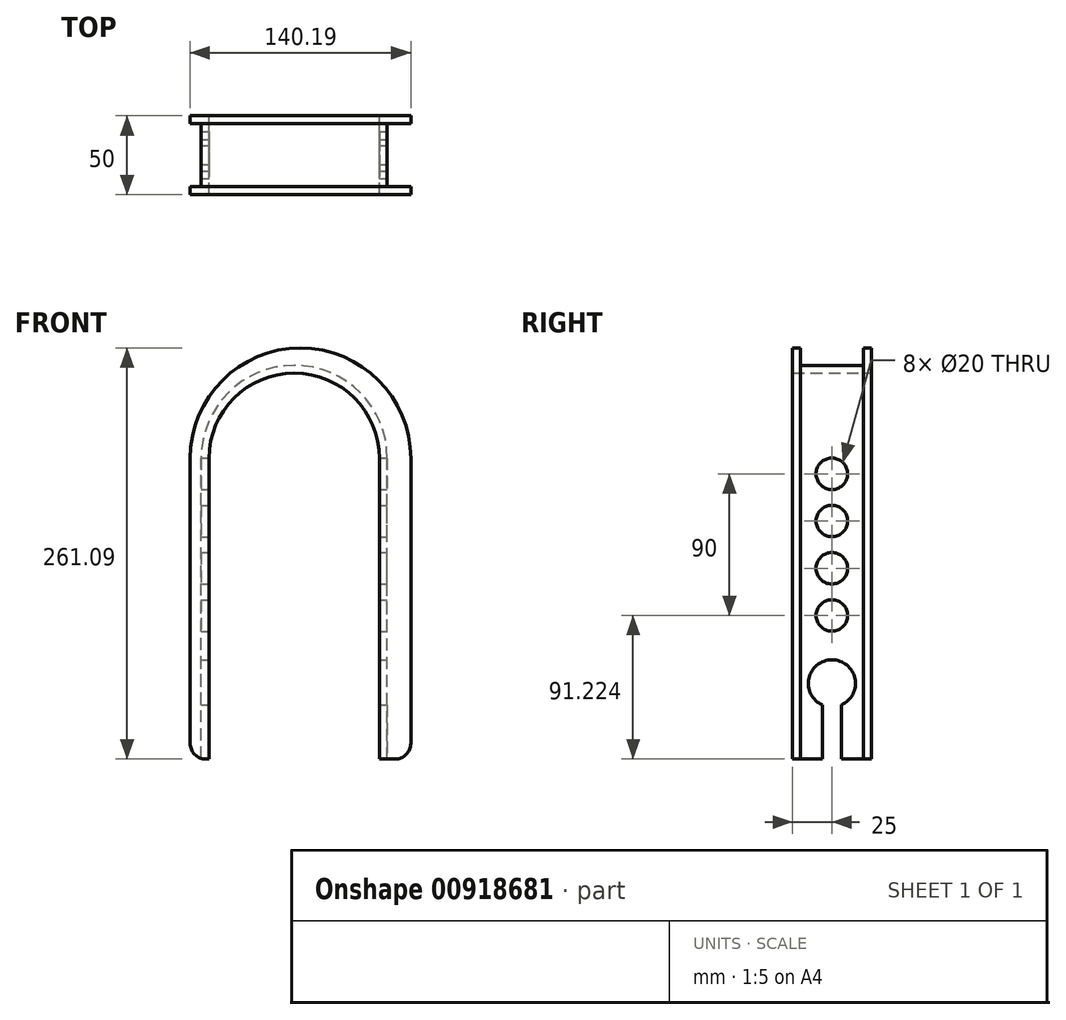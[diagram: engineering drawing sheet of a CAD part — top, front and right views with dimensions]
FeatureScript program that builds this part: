
annotation { "Feature Type Name" : "Feature", "Feature Type Description" : "" }
export const myFeature = defineFeature(function(context is Context, id is Id, definition is map)
    precondition{}
    {
        {
            var Q0;
            Q0=qCreatedBy(makeId("Front.planeOp"),FACE);
            var sketch = newSketch(context, id + "F0", { "sketchPlane" : qUnion([Q0])});
            skLineSegment(sketch, "E0", {"start": v(-68.1, -115.24) * mm, "end": v(-68.1, 65.76) * mm});
            skLineSegment(sketch, "E1", {"start": v(-56.1, -125.24) * mm, "end": v(-56.1, 65.76) * mm});
            skLineSegment(sketch, "E2", {"start": v(52.08, -125.24) * mm, "end": v(52.08, 65.76) * mm});
            skLineSegment(sketch, "E3", {"start": v(72.08, -115.24) * mm, "end": v(72.08, 65.76) * mm});
            skArc(sketch, "E4", {"start": v(52.08, 65.76) * mm, "mid": v(-2.01, 119.85) * mm, "end": v(-56.1, 65.76) * mm});
            skArc(sketch, "E5", {"start": v(72.08, 65.76) * mm, "mid": v(1.99, 135.85) * mm, "end": v(-68.1, 65.76) * mm});
            skLineSegment(sketch, "E6", {"start": v(-58.1, -125.24) * mm, "end": v(-56.1, -125.24) * mm});
            skLineSegment(sketch, "E7", {"start": v(52.08, -125.24) * mm, "end": v(62.08, -125.24) * mm});
            skPoint(sketch, "E8.visualSharp", {"position": v(-68.1, -125.24) * mm});
            skArc(sketch, "E8.filletArc", {"start": v(-68.1, -115.24) * mm, "mid": v(-65.18, -122.31) * mm, "end": v(-58.1, -125.24) * mm});
            skPoint(sketch, "E9.visualSharp", {"position": v(72.08, -125.24) * mm});
            skArc(sketch, "E9.filletArc", {"start": v(62.08, -125.24) * mm, "mid": v(69.15, -122.31) * mm, "end": v(72.08, -115.24) * mm});
            skLineSegment(sketch, "E10", {"start": v(-68.1, 65.76) * mm, "end": v(75.19, 65.76) * mm, "construction": true});
            skLineSegment(sketch, "E11", {"start": v(75.19, 65.76) * mm, "end": v(-68.1, 65.76) * mm, "construction": true});
            skLineSegment(sketch, "E12", {"start": v(-95.5, -125.24) * mm, "end": v(86.96, -125.24) * mm, "construction": true});
            skSolve(sketch);
        }
        {
            var Q0;
            Q0 = qSketchRegion(id + "F0", true);
            extrude(context, id + "F1", {"entities" : qUnion([Q0]), "depth" : 50 * mm, "offsetDistance" : 25 * mm});
        }
        {
            var Q0;
            Q0=makeQuery(id+"F1.opExtrude","SWEPT_FACE",FACE,{"disambiguationData":[OSD([sQuery(id+"F0.wireOp",EDGE,"E0")])]});
            var Q1;
            Q1=makeQuery(id+"F1.opExtrude","SWEPT_FACE",FACE,{"disambiguationData":[OSD([sQuery(id+"F0.wireOp",EDGE,"E5")])]});
            var Q2;
            Q2=makeQuery(id+"F1.opExtrude","SWEPT_FACE",FACE,{"disambiguationData":[OSD([sQuery(id+"F0.wireOp",EDGE,"E3")])]});
            shell(context, id + "F2", {"entities" : qUnion([Q0, Q1, Q2]), "thickness" : 5 * mm});
        }
        {
            var Q0;
            Q0=makeQuery(id+"F2.opShell","OFFSET_FACE",FACE,{"disambiguationData":[OSD([sQuery(id+"F0.wireOp",EDGE,"E2")])]});
            var sketch = newSketch(context, id + "F3", { "sketchPlane" : qUnion([Q0])});
            skPoint(sketch, "E13.centerSnap0", {"position": v(-25, -120.24) * mm});
            skLineSegment(sketch, "E14", {"start": v(9.24, -77.17) * mm, "end": v(-58.42, -77.17) * mm, "construction": true});
            skPoint(sketch, "E13.center.orphan", {"position": v(-25, -77.17) * mm});
            skArc(sketch, "E15", {"start": v(-19, -90.92) * mm, "mid": v(-25, -62.17) * mm, "end": v(-31, -90.92) * mm});
            skLineSegment(sketch, "E16", {"start": v(-31, -90.92) * mm, "end": v(-31, -125.83) * mm});
            skLineSegment(sketch, "E17", {"start": v(-19, -90.92) * mm, "end": v(-19, -125.83) * mm});
            skSolve(sketch);
        }
        {
            var Q0;
            Q0=makeQuery(id+"Fxhhjyly7ikEwcR_1.boolean.opBoolean","MERGE",FACE,{"derivedFrom":[makeQuery(id+"F2.opShell","OFFSET_FACE",FACE,{"disambiguationData":[OSD([sQuery(id+"F0.wireOp",EDGE,"E2")])]})],"fromTools":[makeQuery(id+"Fxhhjyly7ikEwcR_1.opExtrude","CAP_FACE",FACE,{"disambiguationData":[OSD([sQuery(id+"F0.wireOp",EDGE,"E3"),sQuery(id+"F0.wireOp",EDGE,"E7"),sQuery(id+"FfAtlhIJGWQoZcc_1.wireOp",EDGE,"lfH36EOl-3g7w-Wpb9-1w7m-nU63kjSk3KXv"),sQuery(id+"FfAtlhIJGWQoZcc_1.wireOp",EDGE,"4ROan0Rv-7vJr-hjll-RH8p-9FkXIwtYWzqe")])],"isStart":false})]});
            var sketch = newSketch(context, id + "F4", { "sketchPlane" : qUnion([Q0])});
            skCircle(sketch, "E18", {"center": v(-25, 55.98) * mm, "radius": 10 * mm});
            skPoint(sketch, "E18.centerSnap0", {"position": v(-25, 65.76) * mm});
            skCircle(sketch, "E19", {"center": v(-25, 25.98) * mm, "radius": 10 * mm});
            skCircle(sketch, "E20", {"center": v(-25, -4.02) * mm, "radius": 10 * mm});
            skCircle(sketch, "E21", {"center": v(-25, -34.02) * mm, "radius": 10 * mm});
            skSolve(sketch);
        }
        {
            var Q0;
            Q0 = qSketchRegion(id + "F4", true);
            extrude(context, id + "F5", {"entities" : qUnion([Q0]), "operationType" : NewBodyOperationType.REMOVE, "endBound" : BoundingType.THROUGH_ALL, "oppositeDirection" : true, "depth" : 25 * mm, "offsetDistance" : 25 * mm});
        }
        {
            var Q0;
            {var subQ0=sQuery(id+"F3.wireOp",EDGE,"kIy298A2-9125-Z2Ld-Neu7-9GqD1DHjDZnT");Q0=makeQuery(id+"F3.imprint","IMPRINT",FACE,{"disambiguationData":[TD([[makeQuery(id+"F3.imprint","IMPRINT",EDGE,{"derivedFrom":subQ0}),1.0]])]});}
            var Q1;
            {var subQ0=sQuery(id+"F3.wireOp",EDGE,"E15");Q1=makeQuery(id+"F3.imprint","IMPRINT",FACE,{"disambiguationData":[TD([[makeQuery(id+"F3.imprint","IMPRINT",EDGE,{"derivedFrom":subQ0}),1.0]])]});}
            extrude(context, id + "F6", {"entities" : qUnion([Q0, Q1]), "operationType" : NewBodyOperationType.REMOVE, "endBound" : BoundingType.THROUGH_ALL, "oppositeDirection" : true, "depth" : 25 * mm, "offsetDistance" : 25 * mm});
        }
        {
            var Q0;
            Q0=makeQuery(id+"F1.opExtrude","SWEPT_FACE",FACE,{"disambiguationData":[OSD([sQuery(id+"F0.wireOp",EDGE,"E3")])]});
            var sketch = newSketch(context, id + "F7", { "sketchPlane" : qUnion([Q0])});
            skLineSegment(sketch, "E22.bottom", {"start": v(-45, -115.24) * mm, "end": v(-5, -115.24) * mm});
            skLineSegment(sketch, "E22.top", {"start": v(-45, -125.24) * mm, "end": v(-5, -125.24) * mm});
            skLineSegment(sketch, "E22.left", {"start": v(-45, -115.24) * mm, "end": v(-45, -125.24) * mm});
            skLineSegment(sketch, "E22.right", {"start": v(-5, -115.24) * mm, "end": v(-5, -125.24) * mm});
            skSolve(sketch);
        }
        {
            var Q0;
            Q0=makeQuery(id+"F7.imprint","IMPRINT",FACE,{"disambiguationData":[TD([[makeQuery(id+"F7.imprint","IMPRINT",EDGE,{"derivedFrom":sQuery(id+"F7.wireOp",EDGE,"E22.bottom")}),-1.0]])]});
            extrude(context, id + "F8", {"entities" : qUnion([Q0]), "operationType" : NewBodyOperationType.REMOVE, "oppositeDirection" : true, "depth" : 15 * mm, "offsetDistance" : 25 * mm});
        }
        {
            var Q0;
            Q0=makeQuery(id+"F2.opShell","OFFSET_FACE",FACE,{"disambiguationData":[OSD([sQuery(id+"F0.wireOp",EDGE,"E0")])]});
            var sketch = newSketch(context, id + "F9", { "sketchPlane" : qUnion([Q0])});
            skLineSegment(sketch, "E23.bottom", {"start": v(5, -115.24) * mm, "end": v(45, -115.24) * mm});
            skLineSegment(sketch, "E23.top", {"start": v(5, -125.24) * mm, "end": v(45, -125.24) * mm});
            skLineSegment(sketch, "E23.left", {"start": v(5, -115.24) * mm, "end": v(5, -125.24) * mm});
            skLineSegment(sketch, "E23.right", {"start": v(45, -115.24) * mm, "end": v(45, -125.24) * mm});
            skSolve(sketch);
        }
        {
            var Q0;
            Q0 = qSketchRegion(id + "F9", true);
            extrude(context, id + "F10", {"entities" : qUnion([Q0]), "operationType" : NewBodyOperationType.REMOVE, "oppositeDirection" : true, "depth" : 7 * mm, "offsetDistance" : 25 * mm});
        }
        {
            var Q0;
            Q0=makeQuery(id+"F8.boolean.opBoolean","MERGE",FACE,{"derivedFrom":[makeQuery(id+"F2.opShell","OFFSET_FACE",FACE,{"disambiguationData":[OSD([sQuery(id+"F0.wireOp",EDGE,"E2")])]})],"fromTools":[makeQuery(id+"F8.opExtrude","CAP_FACE",FACE,{"disambiguationData":[OSD([sQuery(id+"F7.wireOp",EDGE,"E22.bottom"),sQuery(id+"F7.wireOp",EDGE,"E22.top"),sQuery(id+"F7.wireOp",EDGE,"E22.left"),sQuery(id+"F7.wireOp",EDGE,"E22.right")])],"isStart":false})]});
            var sketch = newSketch(context, id + "F11", { "sketchPlane" : qUnion([Q0])});
            skLineSegment(sketch, "E24.bottom", {"start": v(-31, -120.24) * mm, "end": v(-19, -120.24) * mm});
            skLineSegment(sketch, "E24.top", {"start": v(-31, -125.24) * mm, "end": v(-19, -125.24) * mm});
            skLineSegment(sketch, "E24.left", {"start": v(-31, -120.24) * mm, "end": v(-31, -125.24) * mm});
            skLineSegment(sketch, "E24.right", {"start": v(-19, -120.24) * mm, "end": v(-19, -125.24) * mm});
            skSolve(sketch);
        }
        {
            var Q0;
            Q0 = qSketchRegion(id + "F11", true);
            extrude(context, id + "F12", {"entities" : qUnion([Q0]), "operationType" : NewBodyOperationType.REMOVE, "endBound" : BoundingType.THROUGH_ALL, "oppositeDirection" : true, "depth" : 25 * mm, "offsetDistance" : 25 * mm});
        }
    });
